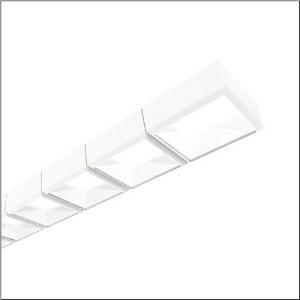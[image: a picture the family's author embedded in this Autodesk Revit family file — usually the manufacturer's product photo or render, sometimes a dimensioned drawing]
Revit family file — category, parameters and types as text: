
# Revit family: scriptus_r__11_5mz312d0twb_510a
name_source: partatom
category: Lighting Fixtures
units: mm (PartAtom-declared; Revit-internal decimal feet)

## family parameters
Cut with Voids When Loaded = No
Host = Face
Light Source = No
Part Type = Normal
Room Calculation Point = No
Round Connector Dimension = Use Diameter
Shared = No

## types (1)
- --- (1 x LED 3000K+6500K / CRI = 80 (unbekannt), 3200 lm / 2380 lm, 3000K)
    Apparent Load = 94 VA
    CIE Flux Codes = 0 0 0 0 100 / 82 95 99 100 100
    Color Rendering = 80
    Color Temperature = 3000K
    Default Elevation = 1800 mm
    Description = Scriptus® 11, office luminaire, primary optical cover: lenses, CAT 2 (L<= 3000cd/m²), light emission: direct/indirect distribution, primary light characteristic: symmetric, installation type: suspended mounting, LED, rated luminous flux: 11.150lm, luminous efficacy: 116lm/W, light colour: 8tw, colour temperature: 3000..6500K, control gear: DALI DT8, with terminal, 5-pole, mains connection: 230V, AC, 50Hz, rated input power: 96W, LED, control gear: ECG DALI, housing, luminaire housing, of aluminium, traffic white (RAL 9016), length: 1.768mm, width: 114mm, height: 57mm, protection rating (complete): IP20, insulation class (complete): insulation class I (protective earthing), certification: CE, protection symbol: F, permissible operating ambient temperature: <= +25°C, standard: EN 50419, packaging unit: 1 piece
    Height = 57 mm
    Lamp = 1 x LED 3000K+6500K / CRI >= 80 (unbekannt)
    Lamp Light Flux = 3200 lm / 2380 lm
    Lamp count = 1
    Length = 1768 mm
    Luminous efficacy = 119 lm/W
    Manufacturer = Siteco
    ModVariant = No
    Model = 5MZ312D0TWB
    Mounting Place = Ceiling
    Mounting Type = Pendant
    Number of Poles = 1
    OnlyDefault = Yes
    Power Factor = 1
    Product Name = Scriptus® 11
    Product group = office luminaire | ceiling pendant
    ProductGroupID = 904
    Protection Class = Protection class I
    Protection Degree = IP 20
    RLX_Detail_Level = 1
    RLX_Emergency_Light_Flux = 0 lm
    RLX_Emergency_Type = 0
    RLX_Emergency_Type_DB = No
    RlxData = <blob elided: 31733 chars, md5=66e8bcae>
    Socket = socket
    Standby Power = 0 W
    System Light Flux = 11160 lm
    System Power = 94 W
    Type Comments = individual setting: colour temperature 6500K
    Type Image = l_1004839.jpg
    URL = http://relux.com
    VarID = @adj_203059
    Voltage = 0 V
    Weight = 0.00 kg
    Width = 114 mm

## geometry (parser evidence)
native form markers: Blend x4, Sweep x19
no freeform markers — native parametric forms only
